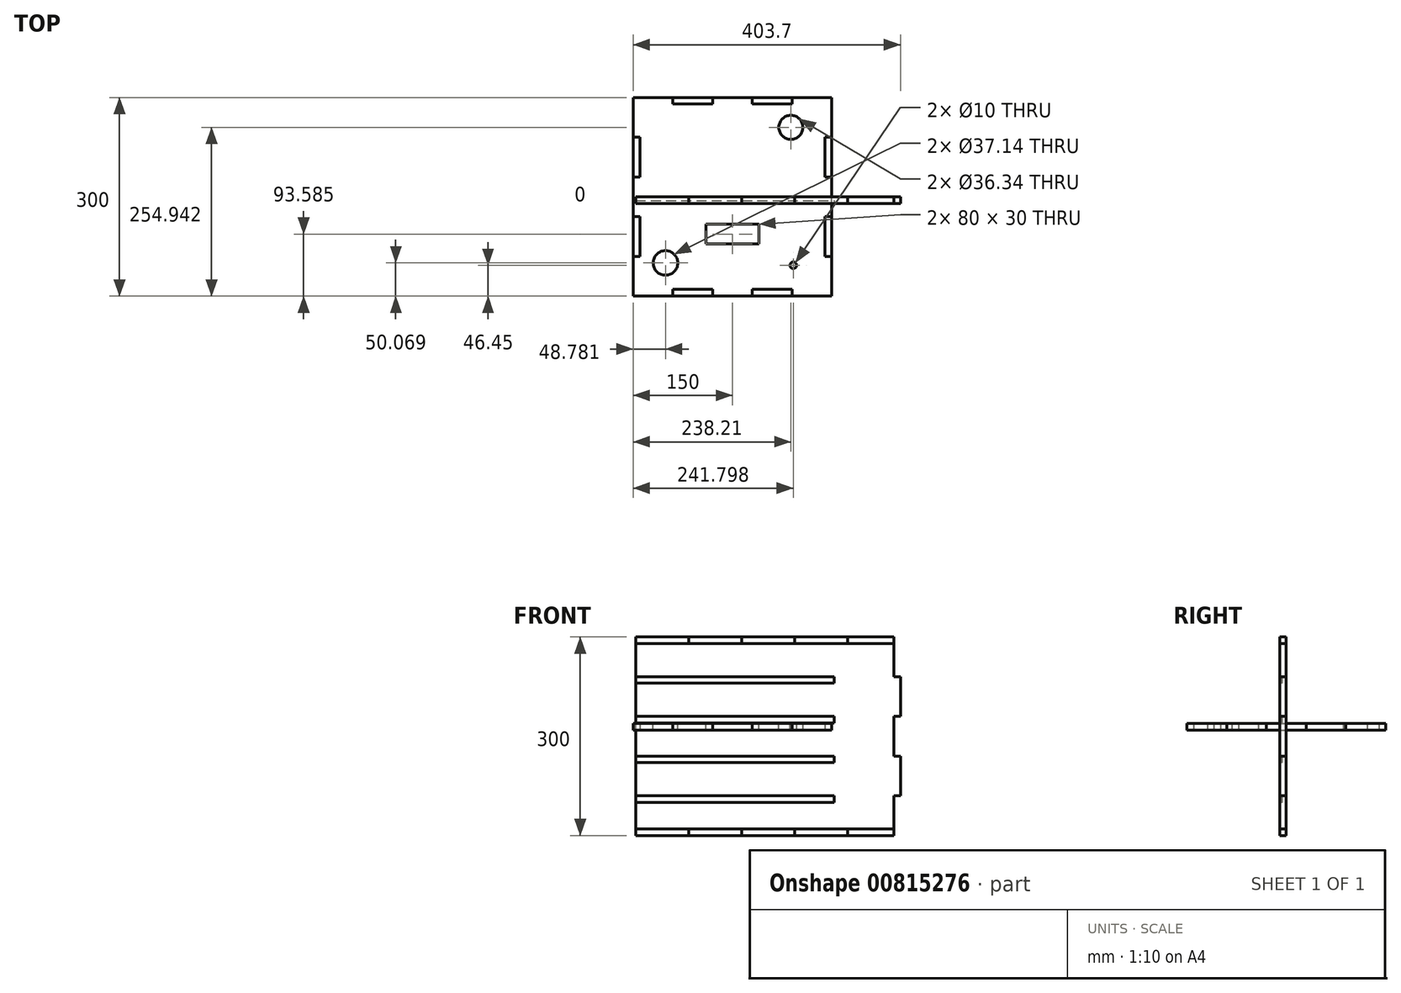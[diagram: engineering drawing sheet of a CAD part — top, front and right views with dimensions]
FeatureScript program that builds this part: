
annotation { "Feature Type Name" : "Feature", "Feature Type Description" : "" }
export const myFeature = defineFeature(function(context is Context, id is Id, definition is map)
    precondition{}
    {
        {
            assignVariable(context, id + "F0", {"name" : "Thickness", "anyValue" : 10 * mm});
        }
        {
            var Q0;
            Q0=qCreatedBy(makeId("Top.planeOp"),FACE);
            var sketch = newSketch(context, id + "F1", { "sketchPlane" : qUnion([Q0])});
            skLineSegment(sketch, "E0.bottom", {"start": v(-150, -150) * mm, "end": v(150, -150) * mm});
            skLineSegment(sketch, "E0.top", {"start": v(-150, 150) * mm, "end": v(150, 150) * mm});
            skLineSegment(sketch, "E0.left", {"start": v(-150, -150) * mm, "end": v(-150, 150) * mm});
            skLineSegment(sketch, "E0.right", {"start": v(150, -150) * mm, "end": v(150, 150) * mm});
            skPoint(sketch, "E0.middle", {"position": v(0, 0) * mm});
            skLineSegment(sketch, "E1", {"start": v(-140, -150) * mm, "end": v(-140, 150) * mm});
            skLineSegment(sketch, "E2", {"start": v(140, 150) * mm, "end": v(140, -150) * mm});
            skLineSegment(sketch, "E3", {"start": v(-150, 140) * mm, "end": v(150, 140) * mm});
            skLineSegment(sketch, "E4", {"start": v(-150, -140) * mm, "end": v(150, -140) * mm});
            skLineSegment(sketch, "E5", {"start": v(-150, 90) * mm, "end": v(-140, 90) * mm});
            skLineSegment(sketch, "E6.0.1.0", {"start": v(-150, 30) * mm, "end": v(-140, 30) * mm});
            skLineSegment(sketch, "E6.0.2.0", {"start": v(-150, -30) * mm, "end": v(-140, -30) * mm});
            skLineSegment(sketch, "E6.0.3.0", {"start": v(-150, -90) * mm, "end": v(-140, -90) * mm});
            skLineSegment(sketch, "E6.direction1", {"start": v(-150, 90) * mm, "end": v(-124.6, 90) * mm, "construction": true});
            skLineSegment(sketch, "E6.direction2", {"start": v(-150, 90) * mm, "end": v(-150, 30) * mm, "construction": true});
            skLineSegment(sketch, "E7", {"start": v(-90, 150) * mm, "end": v(-90, 140) * mm});
            skLineSegment(sketch, "E8.1.0.0", {"start": v(-30, 150) * mm, "end": v(-30, 140) * mm});
            skLineSegment(sketch, "E8.2.0.0", {"start": v(30, 150) * mm, "end": v(30, 140) * mm});
            skLineSegment(sketch, "E8.3.0.0", {"start": v(90, 150) * mm, "end": v(90, 140) * mm});
            skLineSegment(sketch, "E8.direction1", {"start": v(-90, 140) * mm, "end": v(-30, 140) * mm, "construction": true});
            skLineSegment(sketch, "E9", {"start": v(140, 90) * mm, "end": v(150, 90) * mm});
            skLineSegment(sketch, "E10.direction1", {"start": v(140, 90) * mm, "end": v(165.4, 90) * mm, "construction": true});
            skLineSegment(sketch, "E10.direction2", {"start": v(140, 90) * mm, "end": v(140, 30) * mm, "construction": true});
            skLineSegment(sketch, "E11", {"start": v(-90, -140) * mm, "end": v(-90, -150) * mm});
            skLineSegment(sketch, "E12.1.0.0", {"start": v(-30, -140) * mm, "end": v(-30, -150) * mm});
            skLineSegment(sketch, "E12.2.0.0", {"start": v(30, -140) * mm, "end": v(30, -150) * mm});
            skLineSegment(sketch, "E12.3.0.0", {"start": v(90, -140) * mm, "end": v(90, -150) * mm});
            skLineSegment(sketch, "E12.direction1", {"start": v(-90, -150) * mm, "end": v(-30, -150) * mm, "construction": true});
            skLineSegment(sketch, "E13.0.0.1", {"start": v(140, 30) * mm, "end": v(150, 30) * mm});
            skLineSegment(sketch, "E13.0.0.2", {"start": v(140, -30) * mm, "end": v(150, -30) * mm});
            skLineSegment(sketch, "E13.0.0.3", {"start": v(140, -90) * mm, "end": v(150, -90) * mm});
            skSolve(sketch);
        }
        {
            var Q0;
            {var subQ3=sQuery(id+"F1.wireOp",EDGE,"E5");Q0=makeQuery(id+"F1.imprint","IMPRINT",FACE,{"disambiguationData":[TD([[makeQuery(id+"F1.imprint","IMPRINT",EDGE,{"derivedFrom":subQ3}),1.0]])]});}
            var Q1;
            {var subQ0=sQuery(id+"F1.wireOp",EDGE,"E0.left");var subQ1=sQuery(id+"F1.wireOp",EDGE,"E0.top");var subQ2=makeQuery(id+"F1.imprint","INTERSECT",VERTEX,{"derivedFrom":[subQ1,subQ0]});Q1=makeQuery(id+"F1.imprint","IMPRINT",FACE,{"disambiguationData":[TD([[makeQuery(id+"F1.imprint","IMPRINT",EDGE,{"disambiguationData":[TD([[subQ2,-1.0]])],"derivedFrom":subQ1}),-1.0]])]});}
            var Q2;
            {var subQ3=sQuery(id+"F1.wireOp",EDGE,"E7");Q2=makeQuery(id+"F1.imprint","IMPRINT",FACE,{"disambiguationData":[TD([[makeQuery(id+"F1.imprint","IMPRINT",EDGE,{"derivedFrom":subQ3}),-1.0]])]});}
            var Q3;
            {var subQ0=sQuery(id+"F1.wireOp",EDGE,"E8.1.0.0");Q3=makeQuery(id+"F1.imprint","IMPRINT",FACE,{"disambiguationData":[TD([[makeQuery(id+"F1.imprint","IMPRINT",EDGE,{"derivedFrom":subQ0}),1.0]])]});}
            var Q4;
            {var subQ3=sQuery(id+"F1.wireOp",EDGE,"E8.3.0.0");Q4=makeQuery(id+"F1.imprint","IMPRINT",FACE,{"disambiguationData":[TD([[makeQuery(id+"F1.imprint","IMPRINT",EDGE,{"derivedFrom":subQ3}),1.0]])]});}
            var Q5;
            {var subQ0=sQuery(id+"F1.wireOp",EDGE,"E0.right");var subQ1=sQuery(id+"F1.wireOp",EDGE,"E0.top");var subQ2=makeQuery(id+"F1.imprint","INTERSECT",VERTEX,{"derivedFrom":[subQ1,subQ0]});Q5=makeQuery(id+"F1.imprint","IMPRINT",FACE,{"disambiguationData":[TD([[makeQuery(id+"F1.imprint","IMPRINT",EDGE,{"disambiguationData":[TD([[subQ2,1.0]])],"derivedFrom":subQ1}),-1.0]])]});}
            var Q6;
            {var subQ3=sQuery(id+"F1.wireOp",EDGE,"E9");Q6=makeQuery(id+"F1.imprint","IMPRINT",FACE,{"disambiguationData":[TD([[makeQuery(id+"F1.imprint","IMPRINT",EDGE,{"derivedFrom":subQ3}),1.0]])]});}
            var Q7;
            {var subQ0=sQuery(id+"F1.wireOp",EDGE,"E10.0.1.0");Q7=makeQuery(id+"F1.imprint","IMPRINT",FACE,{"disambiguationData":[TD([[makeQuery(id+"F1.imprint","IMPRINT",EDGE,{"derivedFrom":subQ0}),-1.0]])]});}
            var Q8;
            {var subQ3=sQuery(id+"F1.wireOp",EDGE,"E10.0.3.0");Q8=makeQuery(id+"F1.imprint","IMPRINT",FACE,{"disambiguationData":[TD([[makeQuery(id+"F1.imprint","IMPRINT",EDGE,{"derivedFrom":subQ3}),-1.0]])]});}
            var Q9;
            {var subQ0=sQuery(id+"F1.wireOp",EDGE,"E0.right");var subQ1=sQuery(id+"F1.wireOp",EDGE,"E0.bottom");var subQ2=makeQuery(id+"F1.imprint","INTERSECT",VERTEX,{"derivedFrom":[subQ1,subQ0]});Q9=makeQuery(id+"F1.imprint","IMPRINT",FACE,{"disambiguationData":[TD([[makeQuery(id+"F1.imprint","IMPRINT",EDGE,{"disambiguationData":[TD([[subQ2,1.0]])],"derivedFrom":subQ1}),1.0]])]});}
            var Q10;
            {var subQ3=sQuery(id+"F1.wireOp",EDGE,"E12.3.0.0");Q10=makeQuery(id+"F1.imprint","IMPRINT",FACE,{"disambiguationData":[TD([[makeQuery(id+"F1.imprint","IMPRINT",EDGE,{"derivedFrom":subQ3}),1.0]])]});}
            var Q11;
            {var subQ0=sQuery(id+"F1.wireOp",EDGE,"E12.1.0.0");Q11=makeQuery(id+"F1.imprint","IMPRINT",FACE,{"disambiguationData":[TD([[makeQuery(id+"F1.imprint","IMPRINT",EDGE,{"derivedFrom":subQ0}),1.0]])]});}
            var Q12;
            {var subQ3=sQuery(id+"F1.wireOp",EDGE,"E11");Q12=makeQuery(id+"F1.imprint","IMPRINT",FACE,{"disambiguationData":[TD([[makeQuery(id+"F1.imprint","IMPRINT",EDGE,{"derivedFrom":subQ3}),-1.0]])]});}
            var Q13;
            {var subQ0=sQuery(id+"F1.wireOp",EDGE,"E0.left");var subQ1=sQuery(id+"F1.wireOp",EDGE,"E0.bottom");var subQ2=makeQuery(id+"F1.imprint","INTERSECT",VERTEX,{"derivedFrom":[subQ1,subQ0]});Q13=makeQuery(id+"F1.imprint","IMPRINT",FACE,{"disambiguationData":[TD([[makeQuery(id+"F1.imprint","IMPRINT",EDGE,{"disambiguationData":[TD([[subQ2,-1.0]])],"derivedFrom":subQ1}),1.0]])]});}
            var Q14;
            {var subQ3=sQuery(id+"F1.wireOp",EDGE,"E6.0.3.0");Q14=makeQuery(id+"F1.imprint","IMPRINT",FACE,{"disambiguationData":[TD([[makeQuery(id+"F1.imprint","IMPRINT",EDGE,{"derivedFrom":subQ3}),-1.0]])]});}
            var Q15;
            {var subQ0=sQuery(id+"F1.wireOp",EDGE,"E6.0.1.0");Q15=makeQuery(id+"F1.imprint","IMPRINT",FACE,{"disambiguationData":[TD([[makeQuery(id+"F1.imprint","IMPRINT",EDGE,{"derivedFrom":subQ0}),-1.0]])]});}
            var Q16;
            {var subQ7=sQuery(id+"F1.wireOp",EDGE,"E1");var subQ12=makeQuery(id+"F1.imprint","INTERSECT",VERTEX,{"derivedFrom":[subQ7,sQuery(id+"F1.wireOp",EDGE,"E6.0.3.0")]});Q16=makeQuery(id+"F1.imprint","IMPRINT",FACE,{"disambiguationData":[TD([[makeQuery(id+"F1.imprint","IMPRINT",EDGE,{"disambiguationData":[TD([[subQ12,1.0]])],"derivedFrom":subQ7}),-1.0]])]});}
            var Q17;
            {var subQ0=sQuery(id+"F1.wireOp",EDGE,"E13.0.0.1");Q17=makeQuery(id+"F1.imprint","IMPRINT",FACE,{"disambiguationData":[TD([[makeQuery(id+"F1.imprint","IMPRINT",EDGE,{"derivedFrom":subQ0}),-1.0]])]});}
            var Q18;
            {var subQ3=sQuery(id+"F1.wireOp",EDGE,"E13.0.0.3");Q18=makeQuery(id+"F1.imprint","IMPRINT",FACE,{"disambiguationData":[TD([[makeQuery(id+"F1.imprint","IMPRINT",EDGE,{"derivedFrom":subQ3}),-1.0]])]});}
            extrude(context, id + "F2", {"entities" : qUnion([Q0, Q1, Q2, Q3, Q4, Q5, Q6, Q7, Q8, Q9, Q10, Q11, Q12, Q13, Q14, Q15, Q16, Q17, Q18]), "depth" : getVariable(context, 'Thickness'), "offsetDistance" : 25.4 * mm});
        }
        {
            var Q0;
            {var subQ0=sQuery(id+"F1.wireOp",EDGE,"E0.left");var subQ1=sQuery(id+"F1.wireOp",EDGE,"E0.top");var subQ2=makeQuery(id+"F1.imprint","INTERSECT",VERTEX,{"derivedFrom":[subQ1,subQ0]});Q0=makeQuery(id+"F1.imprint","IMPRINT",FACE,{"disambiguationData":[TD([[makeQuery(id+"F1.imprint","IMPRINT",EDGE,{"disambiguationData":[TD([[subQ2,-1.0]])],"derivedFrom":subQ1}),-1.0]])]});}
            var Q1;
            {var subQ3=sQuery(id+"F1.wireOp",EDGE,"E8.3.0.0");Q1=makeQuery(id+"F1.imprint","IMPRINT",FACE,{"disambiguationData":[TD([[makeQuery(id+"F1.imprint","IMPRINT",EDGE,{"derivedFrom":subQ3}),1.0]])]});}
            var Q2;
            {var subQ0=sQuery(id+"F1.wireOp",EDGE,"E6.0.2.0");Q2=makeQuery(id+"F1.imprint","IMPRINT",FACE,{"disambiguationData":[TD([[makeQuery(id+"F1.imprint","IMPRINT",EDGE,{"derivedFrom":subQ0}),-1.0]])]});}
            var Q3;
            {var subQ0=sQuery(id+"F1.wireOp",EDGE,"E9");Q3=makeQuery(id+"F1.imprint","IMPRINT",FACE,{"disambiguationData":[TD([[makeQuery(id+"F1.imprint","IMPRINT",EDGE,{"derivedFrom":subQ0}),-1.0]])]});}
            var Q4;
            {var subQ3=sQuery(id+"F1.wireOp",EDGE,"E6.0.3.0");Q4=makeQuery(id+"F1.imprint","IMPRINT",FACE,{"disambiguationData":[TD([[makeQuery(id+"F1.imprint","IMPRINT",EDGE,{"derivedFrom":subQ3}),-1.0]])]});}
            var Q5;
            {var subQ0=sQuery(id+"F1.wireOp",EDGE,"E6.0.1.0");Q5=makeQuery(id+"F1.imprint","IMPRINT",FACE,{"disambiguationData":[TD([[makeQuery(id+"F1.imprint","IMPRINT",EDGE,{"derivedFrom":subQ0}),-1.0]])]});}
            var Q6;
            {var subQ0=sQuery(id+"F1.wireOp",EDGE,"E0.left");var subQ1=sQuery(id+"F1.wireOp",EDGE,"E0.bottom");var subQ2=makeQuery(id+"F1.imprint","INTERSECT",VERTEX,{"derivedFrom":[subQ1,subQ0]});Q6=makeQuery(id+"F1.imprint","IMPRINT",FACE,{"disambiguationData":[TD([[makeQuery(id+"F1.imprint","IMPRINT",EDGE,{"disambiguationData":[TD([[subQ2,-1.0]])],"derivedFrom":subQ1}),1.0]])]});}
            var Q7;
            {var subQ7=sQuery(id+"F1.wireOp",EDGE,"E1");var subQ12=makeQuery(id+"F1.imprint","INTERSECT",VERTEX,{"derivedFrom":[subQ7,sQuery(id+"F1.wireOp",EDGE,"E6.0.3.0")]});Q7=makeQuery(id+"F1.imprint","IMPRINT",FACE,{"disambiguationData":[TD([[makeQuery(id+"F1.imprint","IMPRINT",EDGE,{"disambiguationData":[TD([[subQ12,1.0]])],"derivedFrom":subQ7}),-1.0]])]});}
            var Q8;
            {var subQ0=sQuery(id+"F1.wireOp",EDGE,"E0.right");var subQ1=sQuery(id+"F1.wireOp",EDGE,"E0.top");var subQ2=makeQuery(id+"F1.imprint","INTERSECT",VERTEX,{"derivedFrom":[subQ1,subQ0]});Q8=makeQuery(id+"F1.imprint","IMPRINT",FACE,{"disambiguationData":[TD([[makeQuery(id+"F1.imprint","IMPRINT",EDGE,{"disambiguationData":[TD([[subQ2,1.0]])],"derivedFrom":subQ1}),-1.0]])]});}
            var Q9;
            {var subQ0=sQuery(id+"F1.wireOp",EDGE,"E0.right");var subQ1=sQuery(id+"F1.wireOp",EDGE,"E0.bottom");var subQ2=makeQuery(id+"F1.imprint","INTERSECT",VERTEX,{"derivedFrom":[subQ1,subQ0]});Q9=makeQuery(id+"F1.imprint","IMPRINT",FACE,{"disambiguationData":[TD([[makeQuery(id+"F1.imprint","IMPRINT",EDGE,{"disambiguationData":[TD([[subQ2,1.0]])],"derivedFrom":subQ1}),1.0]])]});}
            var Q10;
            {var subQ3=sQuery(id+"F1.wireOp",EDGE,"E11");Q10=makeQuery(id+"F1.imprint","IMPRINT",FACE,{"disambiguationData":[TD([[makeQuery(id+"F1.imprint","IMPRINT",EDGE,{"derivedFrom":subQ3}),-1.0]])]});}
            var Q11;
            {var subQ0=sQuery(id+"F1.wireOp",EDGE,"E11");Q11=makeQuery(id+"F1.imprint","IMPRINT",FACE,{"disambiguationData":[TD([[makeQuery(id+"F1.imprint","IMPRINT",EDGE,{"derivedFrom":subQ0}),1.0]])]});}
            var Q12;
            {var subQ0=sQuery(id+"F1.wireOp",EDGE,"E12.2.0.0");Q12=makeQuery(id+"F1.imprint","IMPRINT",FACE,{"disambiguationData":[TD([[makeQuery(id+"F1.imprint","IMPRINT",EDGE,{"derivedFrom":subQ0}),1.0]])]});}
            var Q13;
            {var subQ0=sQuery(id+"F1.wireOp",EDGE,"E12.1.0.0");Q13=makeQuery(id+"F1.imprint","IMPRINT",FACE,{"disambiguationData":[TD([[makeQuery(id+"F1.imprint","IMPRINT",EDGE,{"derivedFrom":subQ0}),1.0]])]});}
            var Q14;
            {var subQ3=sQuery(id+"F1.wireOp",EDGE,"E7");Q14=makeQuery(id+"F1.imprint","IMPRINT",FACE,{"disambiguationData":[TD([[makeQuery(id+"F1.imprint","IMPRINT",EDGE,{"derivedFrom":subQ3}),-1.0]])]});}
            var Q15;
            {var subQ3=sQuery(id+"F1.wireOp",EDGE,"E12.3.0.0");Q15=makeQuery(id+"F1.imprint","IMPRINT",FACE,{"disambiguationData":[TD([[makeQuery(id+"F1.imprint","IMPRINT",EDGE,{"derivedFrom":subQ3}),1.0]])]});}
            var Q16;
            {var subQ0=sQuery(id+"F1.wireOp",EDGE,"E7");Q16=makeQuery(id+"F1.imprint","IMPRINT",FACE,{"disambiguationData":[TD([[makeQuery(id+"F1.imprint","IMPRINT",EDGE,{"derivedFrom":subQ0}),1.0]])]});}
            var Q17;
            {var subQ0=sQuery(id+"F1.wireOp",EDGE,"E8.1.0.0");Q17=makeQuery(id+"F1.imprint","IMPRINT",FACE,{"disambiguationData":[TD([[makeQuery(id+"F1.imprint","IMPRINT",EDGE,{"derivedFrom":subQ0}),1.0]])]});}
            var Q18;
            {var subQ0=sQuery(id+"F1.wireOp",EDGE,"E10.0.2.0");Q18=makeQuery(id+"F1.imprint","IMPRINT",FACE,{"disambiguationData":[TD([[makeQuery(id+"F1.imprint","IMPRINT",EDGE,{"derivedFrom":subQ0}),-1.0]])]});}
            var Q19;
            {var subQ0=sQuery(id+"F1.wireOp",EDGE,"E8.2.0.0");Q19=makeQuery(id+"F1.imprint","IMPRINT",FACE,{"disambiguationData":[TD([[makeQuery(id+"F1.imprint","IMPRINT",EDGE,{"derivedFrom":subQ0}),1.0]])]});}
            var Q20;
            {var subQ3=sQuery(id+"F1.wireOp",EDGE,"E9");Q20=makeQuery(id+"F1.imprint","IMPRINT",FACE,{"disambiguationData":[TD([[makeQuery(id+"F1.imprint","IMPRINT",EDGE,{"derivedFrom":subQ3}),1.0]])]});}
            var Q21;
            {var subQ0=sQuery(id+"F1.wireOp",EDGE,"E10.0.1.0");Q21=makeQuery(id+"F1.imprint","IMPRINT",FACE,{"disambiguationData":[TD([[makeQuery(id+"F1.imprint","IMPRINT",EDGE,{"derivedFrom":subQ0}),-1.0]])]});}
            var Q22;
            {var subQ0=sQuery(id+"F1.wireOp",EDGE,"E5");Q22=makeQuery(id+"F1.imprint","IMPRINT",FACE,{"disambiguationData":[TD([[makeQuery(id+"F1.imprint","IMPRINT",EDGE,{"derivedFrom":subQ0}),-1.0]])]});}
            var Q23;
            {var subQ3=sQuery(id+"F1.wireOp",EDGE,"E10.0.3.0");Q23=makeQuery(id+"F1.imprint","IMPRINT",FACE,{"disambiguationData":[TD([[makeQuery(id+"F1.imprint","IMPRINT",EDGE,{"derivedFrom":subQ3}),-1.0]])]});}
            var Q24;
            {var subQ3=sQuery(id+"F1.wireOp",EDGE,"E5");Q24=makeQuery(id+"F1.imprint","IMPRINT",FACE,{"disambiguationData":[TD([[makeQuery(id+"F1.imprint","IMPRINT",EDGE,{"derivedFrom":subQ3}),1.0]])]});}
            var Q25;
            {var subQ0=sQuery(id+"F1.wireOp",EDGE,"E13.0.0.1");Q25=makeQuery(id+"F1.imprint","IMPRINT",FACE,{"disambiguationData":[TD([[makeQuery(id+"F1.imprint","IMPRINT",EDGE,{"derivedFrom":subQ0}),-1.0]])]});}
            var Q26;
            {var subQ0=sQuery(id+"F1.wireOp",EDGE,"E13.0.0.2");Q26=makeQuery(id+"F1.imprint","IMPRINT",FACE,{"disambiguationData":[TD([[makeQuery(id+"F1.imprint","IMPRINT",EDGE,{"derivedFrom":subQ0}),-1.0]])]});}
            var Q27;
            {var subQ3=sQuery(id+"F1.wireOp",EDGE,"E13.0.0.3");Q27=makeQuery(id+"F1.imprint","IMPRINT",FACE,{"disambiguationData":[TD([[makeQuery(id+"F1.imprint","IMPRINT",EDGE,{"derivedFrom":subQ3}),-1.0]])]});}
            extrude(context, id + "F3", {"entities" : qUnion([Q0, Q1, Q2, Q3, Q4, Q5, Q6, Q7, Q8, Q9, Q10, Q11, Q12, Q13, Q14, Q15, Q16, Q17, Q18, Q19, Q20, Q21, Q22, Q23, Q24, Q25, Q26, Q27]), "depth" : getVariable(context, 'Thickness'), "offsetDistance" : 25.4 * mm});
        }
        {
            var Q0;
            Q0=qCreatedBy(makeId("Front.planeOp"),FACE);
            var sketch = newSketch(context, id + "F4", { "sketchPlane" : qUnion([Q0])});
            skLineSegment(sketch, "E14.bottom", {"start": v(-146.3, -159.35) * mm, "end": v(253.7, -159.35) * mm});
            skLineSegment(sketch, "E14.top", {"start": v(-146.3, 140.65) * mm, "end": v(253.7, 140.65) * mm});
            skLineSegment(sketch, "E14.left", {"start": v(-146.3, -159.35) * mm, "end": v(-146.3, 140.65) * mm});
            skLineSegment(sketch, "E14.right", {"start": v(253.7, -159.35) * mm, "end": v(253.7, 140.65) * mm});
            skPoint(sketch, "E14.middle", {"position": v(53.7, -9.35) * mm});
            skLineSegment(sketch, "E15", {"start": v(-136.3, -159.35) * mm, "end": v(-136.3, 140.65) * mm});
            skLineSegment(sketch, "E16", {"start": v(243.7, 140.65) * mm, "end": v(243.7, -159.35) * mm});
            skLineSegment(sketch, "E17", {"start": v(-146.3, 130.65) * mm, "end": v(253.7, 130.65) * mm});
            skLineSegment(sketch, "E18", {"start": v(-146.3, -149.35) * mm, "end": v(253.7, -149.35) * mm});
            skLineSegment(sketch, "E19", {"start": v(-146.3, 80.65) * mm, "end": v(-136.3, 80.65) * mm});
            skLineSegment(sketch, "E20.0.1.0", {"start": v(-146.3, 20.65) * mm, "end": v(-136.3, 20.65) * mm});
            skLineSegment(sketch, "E20.0.2.0", {"start": v(-146.3, -39.35) * mm, "end": v(-136.3, -39.35) * mm});
            skLineSegment(sketch, "E20.0.3.0", {"start": v(-146.3, -99.35) * mm, "end": v(-136.3, -99.35) * mm});
            skLineSegment(sketch, "E20.direction1", {"start": v(-146.3, 80.65) * mm, "end": v(-120.9, 80.65) * mm, "construction": true});
            skLineSegment(sketch, "E20.direction2", {"start": v(-146.3, 80.65) * mm, "end": v(-146.3, 20.65) * mm, "construction": true});
            skLineSegment(sketch, "E21", {"start": v(-66.3, 140.65) * mm, "end": v(-66.3, 130.65) * mm});
            skLineSegment(sketch, "E22.1.0.0", {"start": v(13.7, 140.65) * mm, "end": v(13.7, 130.65) * mm});
            skLineSegment(sketch, "E22.2.0.0", {"start": v(93.7, 140.65) * mm, "end": v(93.7, 130.65) * mm});
            skLineSegment(sketch, "E22.3.0.0", {"start": v(173.7, 140.65) * mm, "end": v(173.7, 130.65) * mm});
            skLineSegment(sketch, "E22.direction1", {"start": v(-66.3, 130.65) * mm, "end": v(13.7, 130.65) * mm, "construction": true});
            skLineSegment(sketch, "E23", {"start": v(243.7, 80.65) * mm, "end": v(253.7, 80.65) * mm});
            skLineSegment(sketch, "E24.direction1", {"start": v(169.1, 80.65) * mm, "end": v(243.7, 80.65) * mm, "construction": true});
            skLineSegment(sketch, "E24.direction2", {"start": v(243.7, 80.65) * mm, "end": v(243.7, 20.65) * mm, "construction": true});
            skLineSegment(sketch, "E25", {"start": v(-66.3, -149.35) * mm, "end": v(-66.3, -159.35) * mm});
            skLineSegment(sketch, "E26.1.0.0", {"start": v(13.7, -149.35) * mm, "end": v(13.7, -159.35) * mm});
            skLineSegment(sketch, "E26.2.0.0", {"start": v(93.7, -149.35) * mm, "end": v(93.7, -159.35) * mm});
            skLineSegment(sketch, "E26.3.0.0", {"start": v(173.7, -149.35) * mm, "end": v(173.7, -159.35) * mm});
            skLineSegment(sketch, "E26.direction1", {"start": v(-66.3, -159.35) * mm, "end": v(13.7, -159.35) * mm, "construction": true});
            skLineSegment(sketch, "E27.0.0.1", {"start": v(243.7, 20.65) * mm, "end": v(253.7, 20.65) * mm});
            skLineSegment(sketch, "E27.0.0.2", {"start": v(243.7, -39.35) * mm, "end": v(253.7, -39.35) * mm});
            skLineSegment(sketch, "E27.0.0.3", {"start": v(243.7, -99.35) * mm, "end": v(253.7, -99.35) * mm});
            skSolve(sketch);
        }
        {
            var Q0;
            {var subQ3=sQuery(id+"F4.wireOp",EDGE,"E22.3.0.0");Q0=makeQuery(id+"F4.imprint","IMPRINT",FACE,{"disambiguationData":[TD([[makeQuery(id+"F4.imprint","IMPRINT",EDGE,{"derivedFrom":subQ3}),1.0]])]});}
            var Q1;
            {var subQ0=sQuery(id+"F4.wireOp",EDGE,"E23");Q1=makeQuery(id+"F4.imprint","IMPRINT",FACE,{"disambiguationData":[TD([[makeQuery(id+"F4.imprint","IMPRINT",EDGE,{"derivedFrom":subQ0}),-1.0]])]});}
            var Q2;
            {var subQ0=sQuery(id+"F4.wireOp",EDGE,"E27.0.0.2");Q2=makeQuery(id+"F4.imprint","IMPRINT",FACE,{"disambiguationData":[TD([[makeQuery(id+"F4.imprint","IMPRINT",EDGE,{"derivedFrom":subQ0}),-1.0]])]});}
            var Q3;
            {var subQ3=sQuery(id+"F4.wireOp",EDGE,"E26.3.0.0");Q3=makeQuery(id+"F4.imprint","IMPRINT",FACE,{"disambiguationData":[TD([[makeQuery(id+"F4.imprint","IMPRINT",EDGE,{"derivedFrom":subQ3}),1.0]])]});}
            var Q4;
            {var subQ0=sQuery(id+"F4.wireOp",EDGE,"E26.1.0.0");Q4=makeQuery(id+"F4.imprint","IMPRINT",FACE,{"disambiguationData":[TD([[makeQuery(id+"F4.imprint","IMPRINT",EDGE,{"derivedFrom":subQ0}),1.0]])]});}
            var Q5;
            {var subQ3=sQuery(id+"F4.wireOp",EDGE,"E25");Q5=makeQuery(id+"F4.imprint","IMPRINT",FACE,{"disambiguationData":[TD([[makeQuery(id+"F4.imprint","IMPRINT",EDGE,{"derivedFrom":subQ3}),-1.0]])]});}
            var Q6;
            {var subQ0=sQuery(id+"F4.wireOp",EDGE,"E14.left");var subQ1=sQuery(id+"F4.wireOp",EDGE,"E14.top");var subQ2=makeQuery(id+"F4.imprint","INTERSECT",VERTEX,{"derivedFrom":[subQ1,subQ0]});Q6=makeQuery(id+"F4.imprint","IMPRINT",FACE,{"disambiguationData":[TD([[makeQuery(id+"F4.imprint","IMPRINT",EDGE,{"disambiguationData":[TD([[subQ2,-1.0]])],"derivedFrom":subQ1}),-1.0]])]});}
            var Q7;
            {var subQ0=sQuery(id+"F4.wireOp",EDGE,"E14.left");var subQ1=sQuery(id+"F4.wireOp",EDGE,"E14.bottom");var subQ2=makeQuery(id+"F4.imprint","INTERSECT",VERTEX,{"derivedFrom":[subQ1,subQ0]});Q7=makeQuery(id+"F4.imprint","IMPRINT",FACE,{"disambiguationData":[TD([[makeQuery(id+"F4.imprint","IMPRINT",EDGE,{"disambiguationData":[TD([[subQ2,-1.0]])],"derivedFrom":subQ1}),1.0]])]});}
            var Q8;
            {var subQ3=sQuery(id+"F4.wireOp",EDGE,"E20.0.3.0");Q8=makeQuery(id+"F4.imprint","IMPRINT",FACE,{"disambiguationData":[TD([[makeQuery(id+"F4.imprint","IMPRINT",EDGE,{"derivedFrom":subQ3}),-1.0]])]});}
            var Q9;
            {var subQ0=sQuery(id+"F4.wireOp",EDGE,"E19");Q9=makeQuery(id+"F4.imprint","IMPRINT",FACE,{"disambiguationData":[TD([[makeQuery(id+"F4.imprint","IMPRINT",EDGE,{"derivedFrom":subQ0}),-1.0]])]});}
            var Q10;
            {var subQ3=sQuery(id+"F4.wireOp",EDGE,"E21");Q10=makeQuery(id+"F4.imprint","IMPRINT",FACE,{"disambiguationData":[TD([[makeQuery(id+"F4.imprint","IMPRINT",EDGE,{"derivedFrom":subQ3}),-1.0]])]});}
            var Q11;
            {var subQ7=sQuery(id+"F4.wireOp",EDGE,"E15");var subQ12=makeQuery(id+"F4.imprint","INTERSECT",VERTEX,{"derivedFrom":[subQ7,sQuery(id+"F4.wireOp",EDGE,"E20.0.3.0")]});Q11=makeQuery(id+"F4.imprint","IMPRINT",FACE,{"disambiguationData":[TD([[makeQuery(id+"F4.imprint","IMPRINT",EDGE,{"disambiguationData":[TD([[subQ12,1.0]])],"derivedFrom":subQ7}),-1.0]])]});}
            var Q12;
            {var subQ3=sQuery(id+"F4.wireOp",EDGE,"E19");Q12=makeQuery(id+"F4.imprint","IMPRINT",FACE,{"disambiguationData":[TD([[makeQuery(id+"F4.imprint","IMPRINT",EDGE,{"derivedFrom":subQ3}),1.0]])]});}
            var Q13;
            {var subQ0=sQuery(id+"F4.wireOp",EDGE,"E20.0.2.0");Q13=makeQuery(id+"F4.imprint","IMPRINT",FACE,{"disambiguationData":[TD([[makeQuery(id+"F4.imprint","IMPRINT",EDGE,{"derivedFrom":subQ0}),-1.0]])]});}
            var Q14;
            {var subQ0=sQuery(id+"F4.wireOp",EDGE,"E20.0.1.0");Q14=makeQuery(id+"F4.imprint","IMPRINT",FACE,{"disambiguationData":[TD([[makeQuery(id+"F4.imprint","IMPRINT",EDGE,{"derivedFrom":subQ0}),-1.0]])]});}
            var Q15;
            {var subQ0=sQuery(id+"F4.wireOp",EDGE,"E22.1.0.0");Q15=makeQuery(id+"F4.imprint","IMPRINT",FACE,{"disambiguationData":[TD([[makeQuery(id+"F4.imprint","IMPRINT",EDGE,{"derivedFrom":subQ0}),1.0]])]});}
            extrude(context, id + "F5", {"entities" : qUnion([Q0, Q1, Q2, Q3, Q4, Q5, Q6, Q7, Q8, Q9, Q10, Q11, Q12, Q13, Q14, Q15]), "depth" : getVariable(context, 'Thickness'), "offsetDistance" : 25.4 * mm});
        }
        {
            var Q0;
            {var subQ3=sQuery(id+"F4.wireOp",EDGE,"E19");Q0=makeQuery(id+"F4.imprint","IMPRINT",FACE,{"disambiguationData":[TD([[makeQuery(id+"F4.imprint","IMPRINT",EDGE,{"derivedFrom":subQ3}),1.0]])]});}
            var Q1;
            {var subQ0=sQuery(id+"F4.wireOp",EDGE,"E20.0.1.0");Q1=makeQuery(id+"F4.imprint","IMPRINT",FACE,{"disambiguationData":[TD([[makeQuery(id+"F4.imprint","IMPRINT",EDGE,{"derivedFrom":subQ0}),-1.0]])]});}
            var Q2;
            {var subQ3=sQuery(id+"F4.wireOp",EDGE,"E20.0.3.0");Q2=makeQuery(id+"F4.imprint","IMPRINT",FACE,{"disambiguationData":[TD([[makeQuery(id+"F4.imprint","IMPRINT",EDGE,{"derivedFrom":subQ3}),-1.0]])]});}
            var Q3;
            {var subQ0=sQuery(id+"F4.wireOp",EDGE,"E19");Q3=makeQuery(id+"F4.imprint","IMPRINT",FACE,{"disambiguationData":[TD([[makeQuery(id+"F4.imprint","IMPRINT",EDGE,{"derivedFrom":subQ0}),-1.0]])]});}
            var Q4;
            {var subQ0=sQuery(id+"F4.wireOp",EDGE,"E20.0.2.0");Q4=makeQuery(id+"F4.imprint","IMPRINT",FACE,{"disambiguationData":[TD([[makeQuery(id+"F4.imprint","IMPRINT",EDGE,{"derivedFrom":subQ0}),-1.0]])]});}
            var Q5;
            {var subQ0=sQuery(id+"F4.wireOp",EDGE,"E21");Q5=makeQuery(id+"F4.imprint","IMPRINT",FACE,{"disambiguationData":[TD([[makeQuery(id+"F4.imprint","IMPRINT",EDGE,{"derivedFrom":subQ0}),1.0]])]});}
            var Q6;
            {var subQ0=sQuery(id+"F4.wireOp",EDGE,"E22.2.0.0");Q6=makeQuery(id+"F4.imprint","IMPRINT",FACE,{"disambiguationData":[TD([[makeQuery(id+"F4.imprint","IMPRINT",EDGE,{"derivedFrom":subQ0}),1.0]])]});}
            var Q7;
            {var subQ0=sQuery(id+"F4.wireOp",EDGE,"E27.0.0.2");Q7=makeQuery(id+"F4.imprint","IMPRINT",FACE,{"disambiguationData":[TD([[makeQuery(id+"F4.imprint","IMPRINT",EDGE,{"derivedFrom":subQ0}),-1.0]])]});}
            var Q8;
            {var subQ0=sQuery(id+"F4.wireOp",EDGE,"E23");Q8=makeQuery(id+"F4.imprint","IMPRINT",FACE,{"disambiguationData":[TD([[makeQuery(id+"F4.imprint","IMPRINT",EDGE,{"derivedFrom":subQ0}),-1.0]])]});}
            var Q9;
            {var subQ0=sQuery(id+"F4.wireOp",EDGE,"E26.2.0.0");Q9=makeQuery(id+"F4.imprint","IMPRINT",FACE,{"disambiguationData":[TD([[makeQuery(id+"F4.imprint","IMPRINT",EDGE,{"derivedFrom":subQ0}),1.0]])]});}
            var Q10;
            {var subQ0=sQuery(id+"F4.wireOp",EDGE,"E25");Q10=makeQuery(id+"F4.imprint","IMPRINT",FACE,{"disambiguationData":[TD([[makeQuery(id+"F4.imprint","IMPRINT",EDGE,{"derivedFrom":subQ0}),1.0]])]});}
            var Q11;
            {var subQ7=sQuery(id+"F4.wireOp",EDGE,"E15");var subQ12=makeQuery(id+"F4.imprint","INTERSECT",VERTEX,{"derivedFrom":[subQ7,sQuery(id+"F4.wireOp",EDGE,"E20.0.3.0")]});Q11=makeQuery(id+"F4.imprint","IMPRINT",FACE,{"disambiguationData":[TD([[makeQuery(id+"F4.imprint","IMPRINT",EDGE,{"disambiguationData":[TD([[subQ12,1.0]])],"derivedFrom":subQ7}),-1.0]])]});}
            extrude(context, id + "F6", {"entities" : qUnion([Q0, Q1, Q2, Q3, Q4, Q5, Q6, Q7, Q8, Q9, Q10, Q11]), "depth" : getVariable(context, 'Thickness'), "offsetDistance" : 25.4 * mm});
        }
        {
            var Q0;
            Q0=makeQuery(id+"F5.opExtrude","CAP_FACE",FACE,{"disambiguationData":[OSD([sQuery(id+"F4.wireOp",EDGE,"E14.bottom"),sQuery(id+"F4.wireOp",EDGE,"E14.top"),sQuery(id+"F4.wireOp",EDGE,"E14.left"),sQuery(id+"F4.wireOp",EDGE,"E14.right"),sQuery(id+"F4.wireOp",EDGE,"E16"),sQuery(id+"F4.wireOp",EDGE,"E17"),sQuery(id+"F4.wireOp",EDGE,"E18"),sQuery(id+"F4.wireOp",EDGE,"E21"),sQuery(id+"F4.wireOp",EDGE,"E22.1.0.0"),sQuery(id+"F4.wireOp",EDGE,"E22.2.0.0"),sQuery(id+"F4.wireOp",EDGE,"E22.3.0.0"),sQuery(id+"F4.wireOp",EDGE,"E23"),sQuery(id+"F4.wireOp",EDGE,"E25"),sQuery(id+"F4.wireOp",EDGE,"E26.1.0.0"),sQuery(id+"F4.wireOp",EDGE,"E26.2.0.0"),sQuery(id+"F4.wireOp",EDGE,"E26.3.0.0"),sQuery(id+"F4.wireOp",EDGE,"E27.0.0.1"),sQuery(id+"F4.wireOp",EDGE,"E27.0.0.2"),sQuery(id+"F4.wireOp",EDGE,"E27.0.0.3")])],"isStart":false});
            var sketch = newSketch(context, id + "F7", { "sketchPlane" : qUnion([Q0])});
            skLineSegment(sketch, "E28.bottom", {"start": v(153.7, 130.65) * mm, "end": v(-146.3, 130.65) * mm});
            skLineSegment(sketch, "E28.top", {"start": v(153.7, -149.35) * mm, "end": v(-146.3, -149.35) * mm});
            skLineSegment(sketch, "E28.left", {"start": v(153.7, 130.65) * mm, "end": v(153.7, -149.35) * mm});
            skLineSegment(sketch, "E28.right", {"start": v(-146.3, 130.65) * mm, "end": v(-146.3, -149.35) * mm});
            skLineSegment(sketch, "E29.bottom", {"start": v(-146.3, 80.65) * mm, "end": v(153.7, 80.65) * mm});
            skLineSegment(sketch, "E29.top", {"start": v(-146.3, 70.65) * mm, "end": v(153.7, 70.65) * mm});
            skLineSegment(sketch, "E29.left", {"start": v(-146.3, 80.65) * mm, "end": v(-146.3, 70.65) * mm});
            skLineSegment(sketch, "E29.right", {"start": v(153.7, 80.65) * mm, "end": v(153.7, 70.65) * mm});
            skLineSegment(sketch, "E30.0.1.0", {"start": v(-146.3, 20.65) * mm, "end": v(153.7, 20.65) * mm});
            skLineSegment(sketch, "E30.0.1.1", {"start": v(-146.3, 10.65) * mm, "end": v(153.7, 10.65) * mm});
            skLineSegment(sketch, "E30.0.2.0", {"start": v(-146.3, -39.35) * mm, "end": v(153.7, -39.35) * mm});
            skLineSegment(sketch, "E30.0.2.1", {"start": v(-146.3, -49.35) * mm, "end": v(153.7, -49.35) * mm});
            skLineSegment(sketch, "E30.0.3.0", {"start": v(-146.3, -99.35) * mm, "end": v(153.7, -99.35) * mm});
            skLineSegment(sketch, "E30.0.3.1", {"start": v(-146.3, -109.35) * mm, "end": v(153.7, -109.35) * mm});
            skLineSegment(sketch, "E30.direction1", {"start": v(-146.3, 80.65) * mm, "end": v(-120.14, 80.65) * mm, "construction": true});
            skLineSegment(sketch, "E30.direction2", {"start": v(-146.3, 80.65) * mm, "end": v(-146.3, 20.65) * mm, "construction": true});
            skSolve(sketch);
        }
        {
            var Q0;
            Q0=makeQuery(id+"F7.imprint","IMPRINT",FACE,{"disambiguationData":[TD([[makeQuery(id+"F7.imprint","IMPRINT",EDGE,{"derivedFrom":sQuery(id+"F7.wireOp",EDGE,"E29.bottom")}),-1.0]])]});
            var Q1;
            {var subQ0=sQuery(id+"F7.wireOp",EDGE,"E30.0.1.0");Q1=makeQuery(id+"F7.imprint","IMPRINT",FACE,{"disambiguationData":[TD([[makeQuery(id+"F7.imprint","IMPRINT",EDGE,{"derivedFrom":subQ0}),-1.0]])]});}
            var Q2;
            {var subQ0=sQuery(id+"F7.wireOp",EDGE,"E30.0.2.0");Q2=makeQuery(id+"F7.imprint","IMPRINT",FACE,{"disambiguationData":[TD([[makeQuery(id+"F7.imprint","IMPRINT",EDGE,{"derivedFrom":subQ0}),-1.0]])]});}
            var Q3;
            {var subQ0=sQuery(id+"F7.wireOp",EDGE,"E30.0.3.0");Q3=makeQuery(id+"F7.imprint","IMPRINT",FACE,{"disambiguationData":[TD([[makeQuery(id+"F7.imprint","IMPRINT",EDGE,{"derivedFrom":subQ0}),-1.0]])]});}
            extrude(context, id + "F8", {"entities" : qUnion([Q0, Q1, Q2, Q3]), "operationType" : NewBodyOperationType.REMOVE, "oppositeDirection" : true, "depth" : 4 * mm, "offsetDistance" : 25.4 * mm});
        }
        {
            var Q0;
            Q0=makeQuery(id+"F2.opExtrude","CAP_FACE",FACE,{"disambiguationData":[OSD([sQuery(id+"F1.wireOp",EDGE,"E0.bottom"),sQuery(id+"F1.wireOp",EDGE,"E0.top"),sQuery(id+"F1.wireOp",EDGE,"E0.left"),sQuery(id+"F1.wireOp",EDGE,"E0.right"),sQuery(id+"F1.wireOp",EDGE,"E1"),sQuery(id+"F1.wireOp",EDGE,"E2"),sQuery(id+"F1.wireOp",EDGE,"E3"),sQuery(id+"F1.wireOp",EDGE,"E4"),sQuery(id+"F1.wireOp",EDGE,"E5"),sQuery(id+"F1.wireOp",EDGE,"E6.0.1.0"),sQuery(id+"F1.wireOp",EDGE,"E6.0.2.0"),sQuery(id+"F1.wireOp",EDGE,"E6.0.3.0"),sQuery(id+"F1.wireOp",EDGE,"E7"),sQuery(id+"F1.wireOp",EDGE,"E8.1.0.0"),sQuery(id+"F1.wireOp",EDGE,"E8.2.0.0"),sQuery(id+"F1.wireOp",EDGE,"E8.3.0.0"),sQuery(id+"F1.wireOp",EDGE,"E9"),sQuery(id+"F1.wireOp",EDGE,"E11"),sQuery(id+"F1.wireOp",EDGE,"E12.1.0.0"),sQuery(id+"F1.wireOp",EDGE,"E12.2.0.0"),sQuery(id+"F1.wireOp",EDGE,"E12.3.0.0"),sQuery(id+"F1.wireOp",EDGE,"E13.0.0.1"),sQuery(id+"F1.wireOp",EDGE,"E13.0.0.2"),sQuery(id+"F1.wireOp",EDGE,"E13.0.0.3")])],"isStart":false});
            var sketch = newSketch(context, id + "F9", { "sketchPlane" : qUnion([Q0])});
            skCircle(sketch, "E31", {"center": v(91.8, -103.55) * mm, "radius": 5 * mm});
            skPoint(sketch, "E31.first.point", {"position": v(95.88, -100.67) * mm});
            skPoint(sketch, "E31.second.point", {"position": v(93.41, -98.82) * mm});
            skPoint(sketch, "E31.third.point", {"position": v(94.54, -99.37) * mm});
            skLineSegment(sketch, "E32.bottom", {"start": v(-40, -41.42) * mm, "end": v(40, -41.42) * mm});
            skLineSegment(sketch, "E32.top", {"start": v(-40, -71.42) * mm, "end": v(40, -71.42) * mm});
            skLineSegment(sketch, "E32.left", {"start": v(-40, -41.42) * mm, "end": v(-40, -71.42) * mm});
            skLineSegment(sketch, "E32.right", {"start": v(40, -41.42) * mm, "end": v(40, -71.42) * mm});
            skCircle(sketch, "E33", {"center": v(88.21, 104.94) * mm, "radius": 18.17 * mm});
            skPoint(sketch, "E33.first.point", {"position": v(105.94, 100.96) * mm});
            skPoint(sketch, "E33.second.point", {"position": v(70.17, 102.8) * mm});
            skPoint(sketch, "E33.third.point", {"position": v(88.1, 123.11) * mm});
            skCircle(sketch, "E34", {"center": v(-101.22, -99.93) * mm, "radius": 18.57 * mm});
            skPoint(sketch, "E34.first.point", {"position": v(-87.8, -112.77) * mm});
            skPoint(sketch, "E34.second.point", {"position": v(-91.18, -84.31) * mm});
            skPoint(sketch, "E34.third.point", {"position": v(-119.42, -103.59) * mm});
            skSolve(sketch);
        }
        {
            var Q0;
            Q0=makeQuery(id+"F9.imprint","IMPRINT",FACE,{"disambiguationData":[TD([[makeQuery(id+"F9.imprint","IMPRINT",EDGE,{"derivedFrom":sQuery(id+"F9.wireOp",EDGE,"E33")}),1.0]])]});
            var Q1;
            Q1=makeQuery(id+"F9.imprint","IMPRINT",FACE,{"disambiguationData":[TD([[makeQuery(id+"F9.imprint","IMPRINT",EDGE,{"derivedFrom":sQuery(id+"F9.wireOp",EDGE,"E32.bottom")}),-1.0]])]});
            var Q2;
            Q2=makeQuery(id+"F9.imprint","IMPRINT",FACE,{"disambiguationData":[TD([[makeQuery(id+"F9.imprint","IMPRINT",EDGE,{"derivedFrom":sQuery(id+"F9.wireOp",EDGE,"E34")}),1.0]])]});
            var Q3;
            Q3=makeQuery(id+"F9.imprint","IMPRINT",FACE,{"disambiguationData":[TD([[makeQuery(id+"F9.imprint","IMPRINT",EDGE,{"derivedFrom":sQuery(id+"F9.wireOp",EDGE,"E31")}),1.0]])]});
            extrude(context, id + "F10", {"entities" : qUnion([Q0, Q1, Q2, Q3]), "operationType" : NewBodyOperationType.REMOVE, "oppositeDirection" : true, "depth" : 10 * mm, "offsetDistance" : 25.4 * mm});
        }
    });
